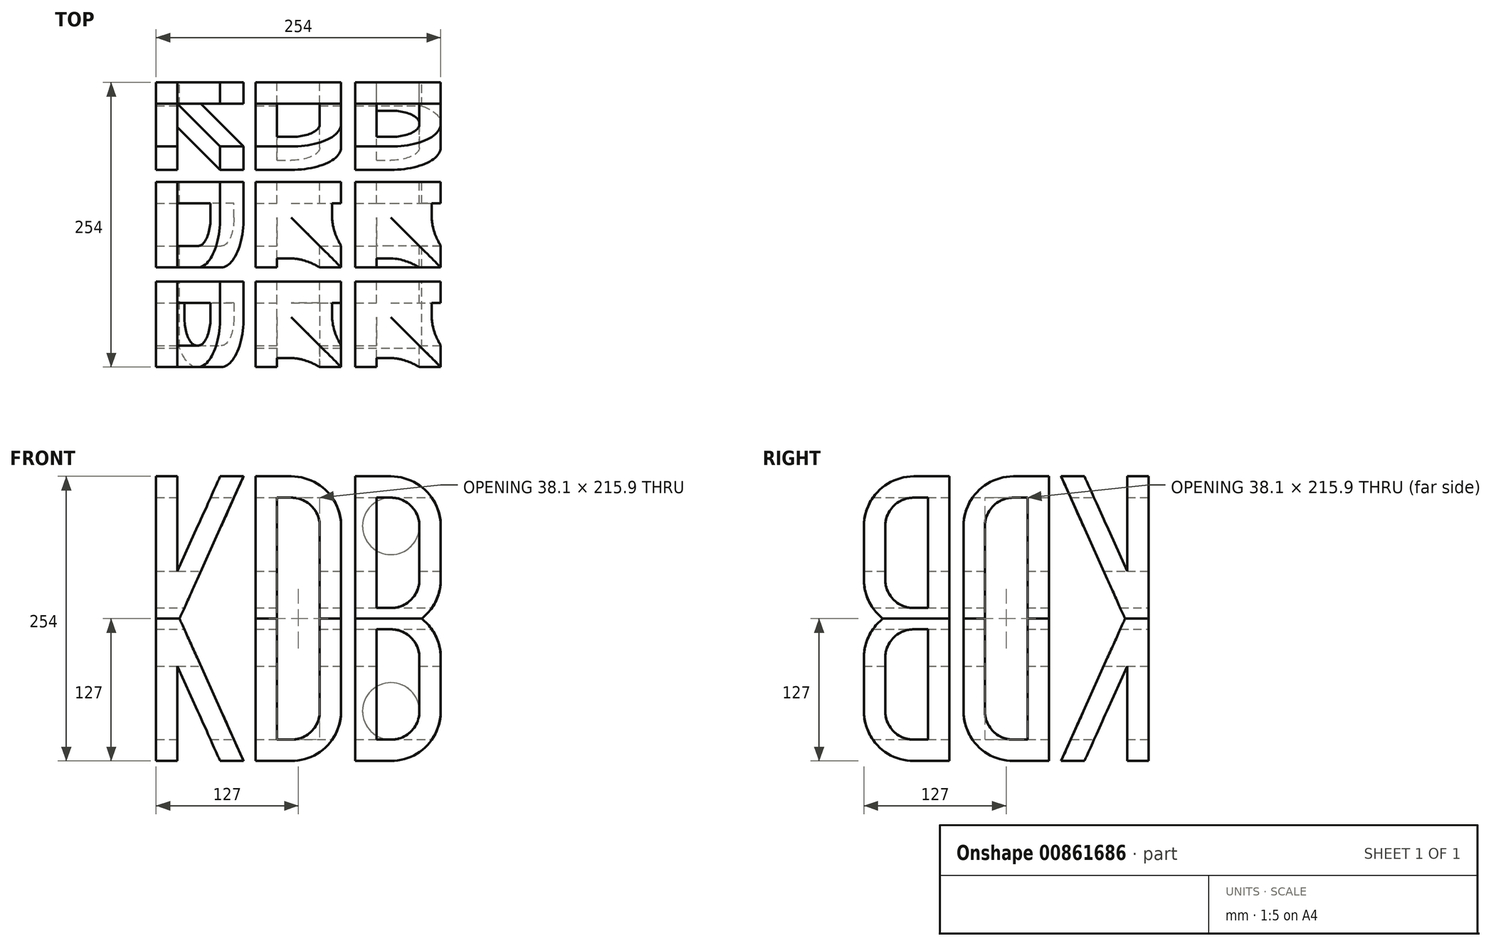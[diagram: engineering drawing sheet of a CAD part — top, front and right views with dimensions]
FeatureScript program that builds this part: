
annotation { "Feature Type Name" : "Feature", "Feature Type Description" : "" }
export const myFeature = defineFeature(function(context is Context, id is Id, definition is map)
    precondition{}
    {
        {
            var Q0;
            Q0=qCreatedBy(makeId("Front.planeOp"),FACE);
            var sketch = newSketch(context, id + "F0", { "sketchPlane" : qUnion([Q0])});
            skLineSegment(sketch, "E0", {"start": v(-107.95, 127) * mm, "end": v(-107.95, 42.33) * mm});
            skLineSegment(sketch, "E1", {"start": v(-69.85, 127) * mm, "end": v(-107.95, 42.33) * mm});
            skPoint(sketch, "E2.orphan", {"position": v(-127, 0) * mm});
            skLineSegment(sketch, "E3", {"start": v(-38.1, 127) * mm, "end": v(-38.1, 0) * mm});
            skLineSegment(sketch, "E4", {"start": v(82.55, 127) * mm, "end": v(50.8, 127) * mm});
            skLineSegment(sketch, "E5", {"start": v(50.8, 127) * mm, "end": v(50.8, 0) * mm});
            skLineSegment(sketch, "E6", {"start": v(69.85, 107.95) * mm, "end": v(69.85, 9.52) * mm});
            skLineSegment(sketch, "E7", {"start": v(107.95, 34.93) * mm, "end": v(107.95, 82.55) * mm});
            skLineSegment(sketch, "E8.0", {"start": v(69.85, 107.95) * mm, "end": v(82.55, 107.95) * mm});
            skLineSegment(sketch, "E9.0", {"start": v(38.1, 82.55) * mm, "end": v(38.1, 0) * mm});
            skLineSegment(sketch, "E10.0", {"start": v(19.05, 82.55) * mm, "end": v(19.05, 0) * mm});
            skLineSegment(sketch, "E11.0", {"start": v(-19.05, 107.95) * mm, "end": v(-19.05, 0) * mm});
            skLineSegment(sketch, "E12.0", {"start": v(69.85, 9.52) * mm, "end": v(82.55, 9.52) * mm});
            skPoint(sketch, "E13.orphan", {"position": v(50.8, 0) * mm});
            skLineSegment(sketch, "E14", {"start": v(127, 34.93) * mm, "end": v(127, 82.55) * mm});
            skArc(sketch, "E15.filletArc", {"start": v(127, 82.55) * mm, "mid": v(113.98, 113.98) * mm, "end": v(82.55, 127) * mm});
            skArc(sketch, "E16.filletArc", {"start": v(107.95, 82.55) * mm, "mid": v(100.51, 100.51) * mm, "end": v(82.55, 107.95) * mm});
            skArc(sketch, "E17.filletArc", {"start": v(110.05, 0) * mm, "mid": v(122.54, 15.51) * mm, "end": v(127, 34.93) * mm});
            skArc(sketch, "E18.filletArc", {"start": v(82.55, 9.52) * mm, "mid": v(100.51, 16.96) * mm, "end": v(107.95, 34.93) * mm});
            skLineSegment(sketch, "E19", {"start": v(-38.1, 127) * mm, "end": v(-6.35, 127) * mm});
            skArc(sketch, "E20.filletArc", {"start": v(38.1, 82.55) * mm, "mid": v(25.08, 113.98) * mm, "end": v(-6.35, 127) * mm});
            skArc(sketch, "E21.0", {"start": v(19.05, 82.55) * mm, "mid": v(11.61, 100.51) * mm, "end": v(-6.35, 107.95) * mm});
            skLineSegment(sketch, "E22", {"start": v(-6.35, 107.95) * mm, "end": v(-19.05, 107.95) * mm});
            skLineSegment(sketch, "E23", {"start": v(-127, 0) * mm, "end": v(127, 0) * mm, "construction": true});
            skLineSegment(sketch, "E24.0", {"start": v(-48.96, 127) * mm, "end": v(-106.11, 0) * mm});
            skLineSegment(sketch, "E25", {"start": v(-69.85, 127) * mm, "end": v(-48.96, 127) * mm});
            skLineSegment(sketch, "E26", {"start": v(-127, 127) * mm, "end": v(-107.95, 127) * mm});
            skLineSegment(sketch, "E27", {"start": v(-127, 127) * mm, "end": v(-127, 0) * mm});
            skArc(sketch, "E28.MirrorCS", {"start": v(110.05, 0) * mm, "mid": v(122.54, -15.51) * mm, "end": v(127, -34.93) * mm});
            skArc(sketch, "E29.MirrorCS", {"start": v(82.55, -9.52) * mm, "mid": v(100.51, -16.96) * mm, "end": v(107.95, -34.93) * mm});
            skLineSegment(sketch, "E30.MirrorCS", {"start": v(107.95, -34.93) * mm, "end": v(107.95, -82.55) * mm});
            skLineSegment(sketch, "E31.MirrorCS", {"start": v(127, -34.92) * mm, "end": v(127, -82.55) * mm});
            skArc(sketch, "E32.MirrorCS", {"start": v(127, -82.55) * mm, "mid": v(113.98, -113.98) * mm, "end": v(82.55, -127) * mm});
            skArc(sketch, "E33.MirrorCS", {"start": v(107.95, -82.55) * mm, "mid": v(100.51, -100.51) * mm, "end": v(82.55, -107.95) * mm});
            skLineSegment(sketch, "E34.MirrorCS", {"start": v(69.85, -107.95) * mm, "end": v(82.55, -107.95) * mm});
            skLineSegment(sketch, "E35.MirrorCS", {"start": v(82.55, -127) * mm, "end": v(50.8, -127) * mm});
            skLineSegment(sketch, "E36.MirrorCS", {"start": v(50.8, -127) * mm, "end": v(50.8, 0) * mm});
            skLineSegment(sketch, "E37.MirrorCS", {"start": v(69.85, -107.95) * mm, "end": v(69.85, -9.52) * mm});
            skLineSegment(sketch, "E38.MirrorCS", {"start": v(69.85, -9.52) * mm, "end": v(82.55, -9.52) * mm});
            skLineSegment(sketch, "E39.MirrorCS", {"start": v(38.1, -82.55) * mm, "end": v(38.1, 0) * mm});
            skLineSegment(sketch, "E40.MirrorCS", {"start": v(19.05, -82.55) * mm, "end": v(19.05, 0) * mm});
            skArc(sketch, "E41.MirrorCS", {"start": v(19.05, -82.55) * mm, "mid": v(11.61, -100.51) * mm, "end": v(-6.35, -107.95) * mm});
            skArc(sketch, "E42.MirrorCS", {"start": v(38.1, -82.55) * mm, "mid": v(25.08, -113.98) * mm, "end": v(-6.35, -127) * mm});
            skLineSegment(sketch, "E43.MirrorCS", {"start": v(-38.1, -127) * mm, "end": v(-6.35, -127) * mm});
            skLineSegment(sketch, "E44.MirrorCS", {"start": v(-6.35, -107.95) * mm, "end": v(-19.05, -107.95) * mm});
            skLineSegment(sketch, "E45.MirrorCS", {"start": v(-19.05, -107.95) * mm, "end": v(-19.05, 0) * mm});
            skLineSegment(sketch, "E46.MirrorCS", {"start": v(-38.1, -127) * mm, "end": v(-38.1, 0) * mm});
            skLineSegment(sketch, "E47.MirrorCS", {"start": v(-48.96, -127) * mm, "end": v(-106.11, 0) * mm});
            skLineSegment(sketch, "E48.MirrorCS", {"start": v(-69.85, -127) * mm, "end": v(-48.96, -127) * mm});
            skLineSegment(sketch, "E49.MirrorCS", {"start": v(-69.85, -127) * mm, "end": v(-107.95, -42.33) * mm});
            skLineSegment(sketch, "E50.MirrorCS", {"start": v(-107.95, -127) * mm, "end": v(-107.95, -42.33) * mm});
            skLineSegment(sketch, "E51.MirrorCS", {"start": v(-127, -127) * mm, "end": v(-107.95, -127) * mm});
            skLineSegment(sketch, "E52.MirrorCS", {"start": v(-127, -127) * mm, "end": v(-127, 0) * mm});
            skLineSegment(sketch, "E53", {"start": v(-196.63, -139.7) * mm, "end": v(280.93, -139.7) * mm, "construction": true});
            skLineSegment(sketch, "E54.MirrorCS", {"start": v(69.85, -269.88) * mm, "end": v(82.55, -269.88) * mm});
            skLineSegment(sketch, "E55.MirrorCS", {"start": v(-6.35, -171.45) * mm, "end": v(-19.05, -171.45) * mm});
            skLineSegment(sketch, "E56.MirrorCS", {"start": v(69.85, -387.35) * mm, "end": v(82.55, -387.35) * mm});
            skLineSegment(sketch, "E57.MirrorCS", {"start": v(69.85, -171.45) * mm, "end": v(82.55, -171.45) * mm});
            skLineSegment(sketch, "E58.MirrorCS", {"start": v(69.85, -288.93) * mm, "end": v(82.55, -288.93) * mm});
            skLineSegment(sketch, "E59.MirrorCS", {"start": v(-6.35, -387.35) * mm, "end": v(-19.05, -387.35) * mm});
            skLineSegment(sketch, "E60.MirrorCS", {"start": v(-69.85, -152.4) * mm, "end": v(-48.96, -152.4) * mm});
            skArc(sketch, "E61.MirrorCS", {"start": v(82.55, -288.93) * mm, "mid": v(100.51, -296.36) * mm, "end": v(107.95, -314.33) * mm});
            skArc(sketch, "E62.MirrorCS", {"start": v(19.05, -361.95) * mm, "mid": v(11.61, -379.91) * mm, "end": v(-6.35, -387.35) * mm});
            skArc(sketch, "E63.MirrorCS", {"start": v(19.05, -196.85) * mm, "mid": v(11.61, -178.89) * mm, "end": v(-6.35, -171.45) * mm});
            skArc(sketch, "E64.MirrorCS", {"start": v(82.55, -269.88) * mm, "mid": v(100.51, -262.44) * mm, "end": v(107.95, -244.47) * mm});
            skArc(sketch, "E65.MirrorCS", {"start": v(107.95, -361.95) * mm, "mid": v(100.51, -379.91) * mm, "end": v(82.55, -387.35) * mm});
            skLineSegment(sketch, "E66.MirrorCS", {"start": v(-107.95, -152.4) * mm, "end": v(-107.95, -237.07) * mm});
            skLineSegment(sketch, "E67.MirrorCS", {"start": v(38.1, -196.85) * mm, "end": v(38.1, -279.4) * mm});
            skLineSegment(sketch, "E68.MirrorCS", {"start": v(107.95, -314.33) * mm, "end": v(107.95, -361.95) * mm});
            skPoint(sketch, "E69.MirrorP", {"position": v(-127, -279.4) * mm});
            skLineSegment(sketch, "E70.MirrorCS", {"start": v(-19.05, -171.45) * mm, "end": v(-19.05, -279.4) * mm});
            skLineSegment(sketch, "E71.MirrorCS", {"start": v(-38.1, -406.4) * mm, "end": v(-38.1, -279.4) * mm});
            skArc(sketch, "E72.MirrorCS", {"start": v(38.1, -361.95) * mm, "mid": v(25.08, -393.38) * mm, "end": v(-6.35, -406.4) * mm});
            skLineSegment(sketch, "E73.MirrorCS", {"start": v(50.8, -406.4) * mm, "end": v(50.8, -279.4) * mm});
            skLineSegment(sketch, "E74.MirrorCS", {"start": v(19.05, -361.95) * mm, "end": v(19.05, -279.4) * mm});
            skPoint(sketch, "E75.MirrorP", {"position": v(127, -152.4) * mm});
            skLineSegment(sketch, "E76.MirrorCS", {"start": v(19.05, -196.85) * mm, "end": v(19.05, -279.4) * mm});
            skLineSegment(sketch, "E77.MirrorCS", {"start": v(107.95, -244.47) * mm, "end": v(107.95, -196.85) * mm});
            skLineSegment(sketch, "E78.MirrorCS", {"start": v(-69.85, -152.4) * mm, "end": v(-107.95, -237.07) * mm});
            skLineSegment(sketch, "E79.MirrorCS", {"start": v(38.1, -361.95) * mm, "end": v(38.1, -279.4) * mm});
            skPoint(sketch, "E80.MirrorP", {"position": v(127, -406.4) * mm});
            skLineSegment(sketch, "E81.MirrorCS", {"start": v(-38.1, -152.4) * mm, "end": v(-38.1, -279.4) * mm});
            skArc(sketch, "E82.MirrorCS", {"start": v(127, -196.85) * mm, "mid": v(113.98, -165.42) * mm, "end": v(82.55, -152.4) * mm});
            skLineSegment(sketch, "E83.MirrorCS", {"start": v(69.85, -387.35) * mm, "end": v(69.85, -288.93) * mm});
            skLineSegment(sketch, "E84.MirrorCS", {"start": v(-127, -279.4) * mm, "end": v(127, -279.4) * mm, "construction": true});
            skLineSegment(sketch, "E85.MirrorCS", {"start": v(-48.96, -152.4) * mm, "end": v(-106.11, -279.4) * mm});
            skPoint(sketch, "E86.MirrorP", {"position": v(50.8, -279.4) * mm});
            skLineSegment(sketch, "E87.MirrorCS", {"start": v(-48.96, -406.4) * mm, "end": v(-106.11, -279.4) * mm});
            skLineSegment(sketch, "E88.MirrorCS", {"start": v(50.8, -152.4) * mm, "end": v(50.8, -279.4) * mm});
            skLineSegment(sketch, "E89.MirrorCS", {"start": v(-19.05, -387.35) * mm, "end": v(-19.05, -279.4) * mm});
            skLineSegment(sketch, "E90.MirrorCS", {"start": v(-69.85, -406.4) * mm, "end": v(-107.95, -321.73) * mm});
            skLineSegment(sketch, "E91.MirrorCS", {"start": v(-107.95, -406.4) * mm, "end": v(-107.95, -321.73) * mm});
            skArc(sketch, "E92.MirrorCS", {"start": v(110.05, -279.4) * mm, "mid": v(122.54, -294.91) * mm, "end": v(127, -314.32) * mm});
            skArc(sketch, "E93.MirrorCS", {"start": v(127, -361.95) * mm, "mid": v(113.98, -393.38) * mm, "end": v(82.55, -406.4) * mm});
            skArc(sketch, "E94.MirrorCS", {"start": v(38.1, -196.85) * mm, "mid": v(25.08, -165.42) * mm, "end": v(-6.35, -152.4) * mm});
            skLineSegment(sketch, "E95.MirrorCS", {"start": v(69.85, -171.45) * mm, "end": v(69.85, -269.88) * mm});
            skLineSegment(sketch, "E96.MirrorCS", {"start": v(-106.11, -279.4) * mm, "end": v(127, -279.4) * mm, "construction": true});
            skLineSegment(sketch, "E97", {"start": v(-107.95, -152.4) * mm, "end": v(-38.1, -152.4) * mm});
            skLineSegment(sketch, "E98", {"start": v(127, -406.4) * mm, "end": v(127, -361.95) * mm});
            skLineSegment(sketch, "E99", {"start": v(127, -406.4) * mm, "end": v(82.55, -406.4) * mm});
            skPoint(sketch, "E100.MirrorCS.start.orphan", {"position": v(-127, -152.4) * mm});
            skLineSegment(sketch, "E101.trimOffspring", {"start": v(-69.85, -406.4) * mm, "end": v(-107.95, -406.4) * mm});
            skPoint(sketch, "E102.orphan", {"position": v(-127, -406.4) * mm});
            skLineSegment(sketch, "E103.trimOffspring", {"start": v(-6.35, -152.4) * mm, "end": v(50.8, -152.4) * mm});
            skPoint(sketch, "E104.MirrorCS.end.orphan", {"position": v(-6.35, -152.4) * mm});
            skLineSegment(sketch, "E105.trimOffspring", {"start": v(-38.1, -406.4) * mm, "end": v(-48.96, -406.4) * mm});
            skLineSegment(sketch, "E106.trimOffspring", {"start": v(50.8, -406.4) * mm, "end": v(-6.35, -406.4) * mm});
            skLineSegment(sketch, "E107.trimOffspring", {"start": v(127, -314.32) * mm, "end": v(127, -244.47) * mm});
            skLineSegment(sketch, "E108.trimOffspring", {"start": v(127, -196.85) * mm, "end": v(127, -152.4) * mm});
            skLineSegment(sketch, "E109.trimOffspring", {"start": v(82.55, -152.4) * mm, "end": v(127, -152.4) * mm});
            skPoint(sketch, "E110.MirrorCS.end.orphan", {"position": v(50.8, -152.4) * mm});
            skPoint(sketch, "E110.MirrorCS.start.orphan", {"position": v(82.55, -152.4) * mm});
            skArc(sketch, "E111.MirrorCS", {"start": v(110.05, -279.4) * mm, "mid": v(122.54, -263.89) * mm, "end": v(127, -244.47) * mm});
            skArc(sketch, "E112.MirrorCS", {"start": v(107.95, -196.85) * mm, "mid": v(100.51, -178.89) * mm, "end": v(82.55, -171.45) * mm});
            skSolve(sketch);
        }
        {
            var Q0;
            Q0 = qSketchRegion(id + "F0", true);
            extrude(context, id + "F1", {"entities" : qUnion([Q0]), "depth" : 254 * mm, "offsetDistance" : 25.4 * mm});
        }
        {
            var Q0;
            Q0=makeQuery(id+"F1.opExtrude","SWEPT_BODY",BODY,{"disambiguationData":[OSD([sQuery(id+"F0.wireOp",EDGE,"E54.MirrorCS"),sQuery(id+"F0.wireOp",EDGE,"E57.MirrorCS"),sQuery(id+"F0.wireOp",EDGE,"E64.MirrorCS"),sQuery(id+"F0.wireOp",EDGE,"E77.MirrorCS"),sQuery(id+"F0.wireOp",EDGE,"E95.MirrorCS"),sQuery(id+"F0.wireOp",EDGE,"E112.MirrorCS")])]});
            var Q1;
            Q1=makeQuery(id+"F1.opExtrude","SWEPT_BODY",BODY,{"disambiguationData":[OSD([sQuery(id+"F0.wireOp",EDGE,"E93.MirrorCS"),sQuery(id+"F0.wireOp",EDGE,"E98"),sQuery(id+"F0.wireOp",EDGE,"E99")])]});
            var Q2;
            Q2=makeQuery(id+"F1.opExtrude","SWEPT_BODY",BODY,{"disambiguationData":[OSD([sQuery(id+"F0.wireOp",EDGE,"E92.MirrorCS"),sQuery(id+"F0.wireOp",EDGE,"E107.trimOffspring"),sQuery(id+"F0.wireOp",EDGE,"E111.MirrorCS")])]});
            var Q3;
            Q3=makeQuery(id+"F1.opExtrude","SWEPT_BODY",BODY,{"disambiguationData":[OSD([sQuery(id+"F0.wireOp",EDGE,"E90.MirrorCS"),sQuery(id+"F0.wireOp",EDGE,"E91.MirrorCS"),sQuery(id+"F0.wireOp",EDGE,"E101.trimOffspring")])]});
            var Q4;
            Q4=makeQuery(id+"F1.opExtrude","SWEPT_BODY",BODY,{"disambiguationData":[OSD([sQuery(id+"F0.wireOp",EDGE,"E82.MirrorCS"),sQuery(id+"F0.wireOp",EDGE,"E108.trimOffspring"),sQuery(id+"F0.wireOp",EDGE,"E109.trimOffspring")])]});
            var Q5;
            Q5=makeQuery(id+"F1.opExtrude","SWEPT_BODY",BODY,{"disambiguationData":[OSD([sQuery(id+"F0.wireOp",EDGE,"E71.MirrorCS"),sQuery(id+"F0.wireOp",EDGE,"E81.MirrorCS"),sQuery(id+"F0.wireOp",EDGE,"E85.MirrorCS"),sQuery(id+"F0.wireOp",EDGE,"E87.MirrorCS"),sQuery(id+"F0.wireOp",EDGE,"E97"),sQuery(id+"F0.wireOp",EDGE,"E105.trimOffspring")])]});
            var Q6;
            Q6=makeQuery(id+"F1.opExtrude","SWEPT_BODY",BODY,{"disambiguationData":[OSD([sQuery(id+"F0.wireOp",EDGE,"E67.MirrorCS"),sQuery(id+"F0.wireOp",EDGE,"E72.MirrorCS"),sQuery(id+"F0.wireOp",EDGE,"E73.MirrorCS"),sQuery(id+"F0.wireOp",EDGE,"E79.MirrorCS"),sQuery(id+"F0.wireOp",EDGE,"E88.MirrorCS"),sQuery(id+"F0.wireOp",EDGE,"E94.MirrorCS"),sQuery(id+"F0.wireOp",EDGE,"E103.trimOffspring"),sQuery(id+"F0.wireOp",EDGE,"E106.trimOffspring")])]});
            var Q7;
            Q7=makeQuery(id+"F1.opExtrude","SWEPT_BODY",BODY,{"disambiguationData":[OSD([sQuery(id+"F0.wireOp",EDGE,"E66.MirrorCS"),sQuery(id+"F0.wireOp",EDGE,"E78.MirrorCS"),sQuery(id+"F0.wireOp",EDGE,"E97")])]});
            var Q8;
            Q8=makeQuery(id+"F1.opExtrude","SWEPT_BODY",BODY,{"disambiguationData":[OSD([sQuery(id+"F0.wireOp",EDGE,"E56.MirrorCS"),sQuery(id+"F0.wireOp",EDGE,"E58.MirrorCS"),sQuery(id+"F0.wireOp",EDGE,"E61.MirrorCS"),sQuery(id+"F0.wireOp",EDGE,"E65.MirrorCS"),sQuery(id+"F0.wireOp",EDGE,"E68.MirrorCS"),sQuery(id+"F0.wireOp",EDGE,"E83.MirrorCS")])]});
            var Q9;
            Q9=makeQuery(id+"F1.opExtrude","SWEPT_BODY",BODY,{"disambiguationData":[OSD([sQuery(id+"F0.wireOp",EDGE,"E55.MirrorCS"),sQuery(id+"F0.wireOp",EDGE,"E59.MirrorCS"),sQuery(id+"F0.wireOp",EDGE,"E62.MirrorCS"),sQuery(id+"F0.wireOp",EDGE,"E63.MirrorCS"),sQuery(id+"F0.wireOp",EDGE,"E70.MirrorCS"),sQuery(id+"F0.wireOp",EDGE,"E74.MirrorCS"),sQuery(id+"F0.wireOp",EDGE,"E76.MirrorCS"),sQuery(id+"F0.wireOp",EDGE,"E89.MirrorCS")])]});
            var Q10;
            Q10=makeQuery(id+"F1.opExtrude","CAP_EDGE",EDGE,{"disambiguationData":[OSD([sQuery(id+"F0.wireOp",EDGE,"E66.MirrorCS")])],"isStart":false});
            var Q11;
            Q11=makeQuery(id+"F1.opExtrude","CAP_EDGE",EDGE,{"disambiguationData":[OSD([sQuery(id+"F0.wireOp",EDGE,"E27"),sQuery(id+"F0.wireOp",EDGE,"E52.MirrorCS")])],"isStart":false});
            transform(context, id + "F2", {"entities" : qUnion([Q0, Q1, Q2, Q3, Q4, Q5, Q6, Q7, Q8, Q9]), "transformType" : TransformType.ROTATION, "transformAxis" : qUnion([Q10]), "angle" : 90 * degree, "makeCopy" : false});
        }
        {
            var Q0;
            Q0=makeQuery(id+"F1.opExtrude","SWEPT_BODY",BODY,{"disambiguationData":[OSD([sQuery(id+"F0.wireOp",EDGE,"E0"),sQuery(id+"F0.wireOp",EDGE,"E1"),sQuery(id+"F0.wireOp",EDGE,"E24.0"),sQuery(id+"F0.wireOp",EDGE,"E25"),sQuery(id+"F0.wireOp",EDGE,"E26"),sQuery(id+"F0.wireOp",EDGE,"E27"),sQuery(id+"F0.wireOp",EDGE,"E47.MirrorCS"),sQuery(id+"F0.wireOp",EDGE,"E48.MirrorCS"),sQuery(id+"F0.wireOp",EDGE,"E49.MirrorCS"),sQuery(id+"F0.wireOp",EDGE,"E50.MirrorCS"),sQuery(id+"F0.wireOp",EDGE,"E51.MirrorCS"),sQuery(id+"F0.wireOp",EDGE,"E52.MirrorCS")])]});
            var Q1;
            Q1=makeQuery(id+"F1.opExtrude","SWEPT_BODY",BODY,{"disambiguationData":[OSD([sQuery(id+"F0.wireOp",EDGE,"E3"),sQuery(id+"F0.wireOp",EDGE,"E9.0"),sQuery(id+"F0.wireOp",EDGE,"E10.0"),sQuery(id+"F0.wireOp",EDGE,"E11.0"),sQuery(id+"F0.wireOp",EDGE,"E19"),sQuery(id+"F0.wireOp",EDGE,"E20.filletArc"),sQuery(id+"F0.wireOp",EDGE,"E21.0"),sQuery(id+"F0.wireOp",EDGE,"E22"),sQuery(id+"F0.wireOp",EDGE,"E39.MirrorCS"),sQuery(id+"F0.wireOp",EDGE,"E40.MirrorCS"),sQuery(id+"F0.wireOp",EDGE,"E41.MirrorCS"),sQuery(id+"F0.wireOp",EDGE,"E42.MirrorCS"),sQuery(id+"F0.wireOp",EDGE,"E43.MirrorCS"),sQuery(id+"F0.wireOp",EDGE,"E44.MirrorCS"),sQuery(id+"F0.wireOp",EDGE,"E45.MirrorCS"),sQuery(id+"F0.wireOp",EDGE,"E46.MirrorCS")])]});
            var Q2;
            Q2=makeQuery(id+"F1.opExtrude","SWEPT_BODY",BODY,{"disambiguationData":[OSD([sQuery(id+"F0.wireOp",EDGE,"E4"),sQuery(id+"F0.wireOp",EDGE,"E5"),sQuery(id+"F0.wireOp",EDGE,"E6"),sQuery(id+"F0.wireOp",EDGE,"E7"),sQuery(id+"F0.wireOp",EDGE,"E8.0"),sQuery(id+"F0.wireOp",EDGE,"E12.0"),sQuery(id+"F0.wireOp",EDGE,"E14"),sQuery(id+"F0.wireOp",EDGE,"E15.filletArc"),sQuery(id+"F0.wireOp",EDGE,"E16.filletArc"),sQuery(id+"F0.wireOp",EDGE,"E17.filletArc"),sQuery(id+"F0.wireOp",EDGE,"E18.filletArc"),sQuery(id+"F0.wireOp",EDGE,"E28.MirrorCS"),sQuery(id+"F0.wireOp",EDGE,"E29.MirrorCS"),sQuery(id+"F0.wireOp",EDGE,"E30.MirrorCS"),sQuery(id+"F0.wireOp",EDGE,"E31.MirrorCS"),sQuery(id+"F0.wireOp",EDGE,"E32.MirrorCS"),sQuery(id+"F0.wireOp",EDGE,"E33.MirrorCS"),sQuery(id+"F0.wireOp",EDGE,"E34.MirrorCS"),sQuery(id+"F0.wireOp",EDGE,"E35.MirrorCS"),sQuery(id+"F0.wireOp",EDGE,"E36.MirrorCS"),sQuery(id+"F0.wireOp",EDGE,"E37.MirrorCS"),sQuery(id+"F0.wireOp",EDGE,"E38.MirrorCS")])]});
            transform(context, id + "F3", {"entities" : qUnion([Q0, Q1, Q2]), "transformType" : TransformType.TRANSLATION_3D, "dx" : 19.05 * mm, "dy" : -234.95 * mm, "dz" : -279.4 * mm, "makeCopy" : false});
        }
        {
            var Q0;
            Q0=makeQuery(id+"F1.opExtrude","SWEPT_BODY",BODY,{"disambiguationData":[OSD([sQuery(id+"F0.wireOp",EDGE,"E66.MirrorCS"),sQuery(id+"F0.wireOp",EDGE,"E78.MirrorCS"),sQuery(id+"F0.wireOp",EDGE,"E97")])]});
            var Q1;
            Q1=makeQuery(id+"F1.opExtrude","SWEPT_BODY",BODY,{"disambiguationData":[OSD([sQuery(id+"F0.wireOp",EDGE,"E71.MirrorCS"),sQuery(id+"F0.wireOp",EDGE,"E81.MirrorCS"),sQuery(id+"F0.wireOp",EDGE,"E85.MirrorCS"),sQuery(id+"F0.wireOp",EDGE,"E87.MirrorCS"),sQuery(id+"F0.wireOp",EDGE,"E97"),sQuery(id+"F0.wireOp",EDGE,"E105.trimOffspring")])]});
            var Q2;
            Q2=makeQuery(id+"F1.opExtrude","SWEPT_BODY",BODY,{"disambiguationData":[OSD([sQuery(id+"F0.wireOp",EDGE,"E67.MirrorCS"),sQuery(id+"F0.wireOp",EDGE,"E72.MirrorCS"),sQuery(id+"F0.wireOp",EDGE,"E73.MirrorCS"),sQuery(id+"F0.wireOp",EDGE,"E79.MirrorCS"),sQuery(id+"F0.wireOp",EDGE,"E88.MirrorCS"),sQuery(id+"F0.wireOp",EDGE,"E94.MirrorCS"),sQuery(id+"F0.wireOp",EDGE,"E103.trimOffspring"),sQuery(id+"F0.wireOp",EDGE,"E106.trimOffspring")])]});
            var Q3;
            Q3=makeQuery(id+"F1.opExtrude","SWEPT_BODY",BODY,{"disambiguationData":[OSD([sQuery(id+"F0.wireOp",EDGE,"E82.MirrorCS"),sQuery(id+"F0.wireOp",EDGE,"E108.trimOffspring"),sQuery(id+"F0.wireOp",EDGE,"E109.trimOffspring")])]});
            var Q4;
            Q4=makeQuery(id+"F1.opExtrude","SWEPT_BODY",BODY,{"disambiguationData":[OSD([sQuery(id+"F0.wireOp",EDGE,"E92.MirrorCS"),sQuery(id+"F0.wireOp",EDGE,"E107.trimOffspring"),sQuery(id+"F0.wireOp",EDGE,"E111.MirrorCS")])]});
            var Q5;
            Q5=makeQuery(id+"F1.opExtrude","SWEPT_BODY",BODY,{"disambiguationData":[OSD([sQuery(id+"F0.wireOp",EDGE,"E93.MirrorCS"),sQuery(id+"F0.wireOp",EDGE,"E98"),sQuery(id+"F0.wireOp",EDGE,"E99")])]});
            var Q6;
            Q6=makeQuery(id+"F1.opExtrude","SWEPT_BODY",BODY,{"disambiguationData":[OSD([sQuery(id+"F0.wireOp",EDGE,"E90.MirrorCS"),sQuery(id+"F0.wireOp",EDGE,"E91.MirrorCS"),sQuery(id+"F0.wireOp",EDGE,"E101.trimOffspring")])]});
            var Q7;
            Q7=makeQuery(id+"F1.opExtrude","SWEPT_BODY",BODY,{"disambiguationData":[OSD([sQuery(id+"F0.wireOp",EDGE,"E55.MirrorCS"),sQuery(id+"F0.wireOp",EDGE,"E59.MirrorCS"),sQuery(id+"F0.wireOp",EDGE,"E62.MirrorCS"),sQuery(id+"F0.wireOp",EDGE,"E63.MirrorCS"),sQuery(id+"F0.wireOp",EDGE,"E70.MirrorCS"),sQuery(id+"F0.wireOp",EDGE,"E74.MirrorCS"),sQuery(id+"F0.wireOp",EDGE,"E76.MirrorCS"),sQuery(id+"F0.wireOp",EDGE,"E89.MirrorCS")])]});
            var Q8;
            Q8=makeQuery(id+"F1.opExtrude","SWEPT_BODY",BODY,{"disambiguationData":[OSD([sQuery(id+"F0.wireOp",EDGE,"E54.MirrorCS"),sQuery(id+"F0.wireOp",EDGE,"E57.MirrorCS"),sQuery(id+"F0.wireOp",EDGE,"E64.MirrorCS"),sQuery(id+"F0.wireOp",EDGE,"E77.MirrorCS"),sQuery(id+"F0.wireOp",EDGE,"E95.MirrorCS"),sQuery(id+"F0.wireOp",EDGE,"E112.MirrorCS")])]});
            var Q9;
            Q9=makeQuery(id+"F1.opExtrude","SWEPT_BODY",BODY,{"disambiguationData":[OSD([sQuery(id+"F0.wireOp",EDGE,"E56.MirrorCS"),sQuery(id+"F0.wireOp",EDGE,"E58.MirrorCS"),sQuery(id+"F0.wireOp",EDGE,"E61.MirrorCS"),sQuery(id+"F0.wireOp",EDGE,"E65.MirrorCS"),sQuery(id+"F0.wireOp",EDGE,"E68.MirrorCS"),sQuery(id+"F0.wireOp",EDGE,"E83.MirrorCS")])]});
            var Q10;
            Q10=makeQuery(id+"F1.opExtrude","SWEPT_BODY",BODY,{"disambiguationData":[OSD([sQuery(id+"F0.wireOp",EDGE,"E0"),sQuery(id+"F0.wireOp",EDGE,"E1"),sQuery(id+"F0.wireOp",EDGE,"E24.0"),sQuery(id+"F0.wireOp",EDGE,"E25"),sQuery(id+"F0.wireOp",EDGE,"E26"),sQuery(id+"F0.wireOp",EDGE,"E27"),sQuery(id+"F0.wireOp",EDGE,"E47.MirrorCS"),sQuery(id+"F0.wireOp",EDGE,"E48.MirrorCS"),sQuery(id+"F0.wireOp",EDGE,"E49.MirrorCS"),sQuery(id+"F0.wireOp",EDGE,"E50.MirrorCS"),sQuery(id+"F0.wireOp",EDGE,"E51.MirrorCS"),sQuery(id+"F0.wireOp",EDGE,"E52.MirrorCS")])]});
            var Q11;
            Q11=makeQuery(id+"F1.opExtrude","SWEPT_BODY",BODY,{"disambiguationData":[OSD([sQuery(id+"F0.wireOp",EDGE,"E3"),sQuery(id+"F0.wireOp",EDGE,"E9.0"),sQuery(id+"F0.wireOp",EDGE,"E10.0"),sQuery(id+"F0.wireOp",EDGE,"E11.0"),sQuery(id+"F0.wireOp",EDGE,"E19"),sQuery(id+"F0.wireOp",EDGE,"E20.filletArc"),sQuery(id+"F0.wireOp",EDGE,"E21.0"),sQuery(id+"F0.wireOp",EDGE,"E22"),sQuery(id+"F0.wireOp",EDGE,"E39.MirrorCS"),sQuery(id+"F0.wireOp",EDGE,"E40.MirrorCS"),sQuery(id+"F0.wireOp",EDGE,"E41.MirrorCS"),sQuery(id+"F0.wireOp",EDGE,"E42.MirrorCS"),sQuery(id+"F0.wireOp",EDGE,"E43.MirrorCS"),sQuery(id+"F0.wireOp",EDGE,"E44.MirrorCS"),sQuery(id+"F0.wireOp",EDGE,"E45.MirrorCS"),sQuery(id+"F0.wireOp",EDGE,"E46.MirrorCS")])]});
            var Q12;
            Q12=makeQuery(id+"F1.opExtrude","SWEPT_BODY",BODY,{"disambiguationData":[OSD([sQuery(id+"F0.wireOp",EDGE,"E4"),sQuery(id+"F0.wireOp",EDGE,"E5"),sQuery(id+"F0.wireOp",EDGE,"E6"),sQuery(id+"F0.wireOp",EDGE,"E7"),sQuery(id+"F0.wireOp",EDGE,"E8.0"),sQuery(id+"F0.wireOp",EDGE,"E12.0"),sQuery(id+"F0.wireOp",EDGE,"E14"),sQuery(id+"F0.wireOp",EDGE,"E15.filletArc"),sQuery(id+"F0.wireOp",EDGE,"E16.filletArc"),sQuery(id+"F0.wireOp",EDGE,"E17.filletArc"),sQuery(id+"F0.wireOp",EDGE,"E18.filletArc"),sQuery(id+"F0.wireOp",EDGE,"E28.MirrorCS"),sQuery(id+"F0.wireOp",EDGE,"E29.MirrorCS"),sQuery(id+"F0.wireOp",EDGE,"E30.MirrorCS"),sQuery(id+"F0.wireOp",EDGE,"E31.MirrorCS"),sQuery(id+"F0.wireOp",EDGE,"E32.MirrorCS"),sQuery(id+"F0.wireOp",EDGE,"E33.MirrorCS"),sQuery(id+"F0.wireOp",EDGE,"E34.MirrorCS"),sQuery(id+"F0.wireOp",EDGE,"E35.MirrorCS"),sQuery(id+"F0.wireOp",EDGE,"E36.MirrorCS"),sQuery(id+"F0.wireOp",EDGE,"E37.MirrorCS"),sQuery(id+"F0.wireOp",EDGE,"E38.MirrorCS")])]});
            booleanBodies(context, id + "F4", {"operationType" : BooleanOperationType.SUBTRACTION, "tools" : qUnion([Q0, Q1, Q2, Q3, Q4, Q5, Q6, Q7, Q8, Q9]), "targets" : qUnion([Q10, Q11, Q12])});
        }
    });
